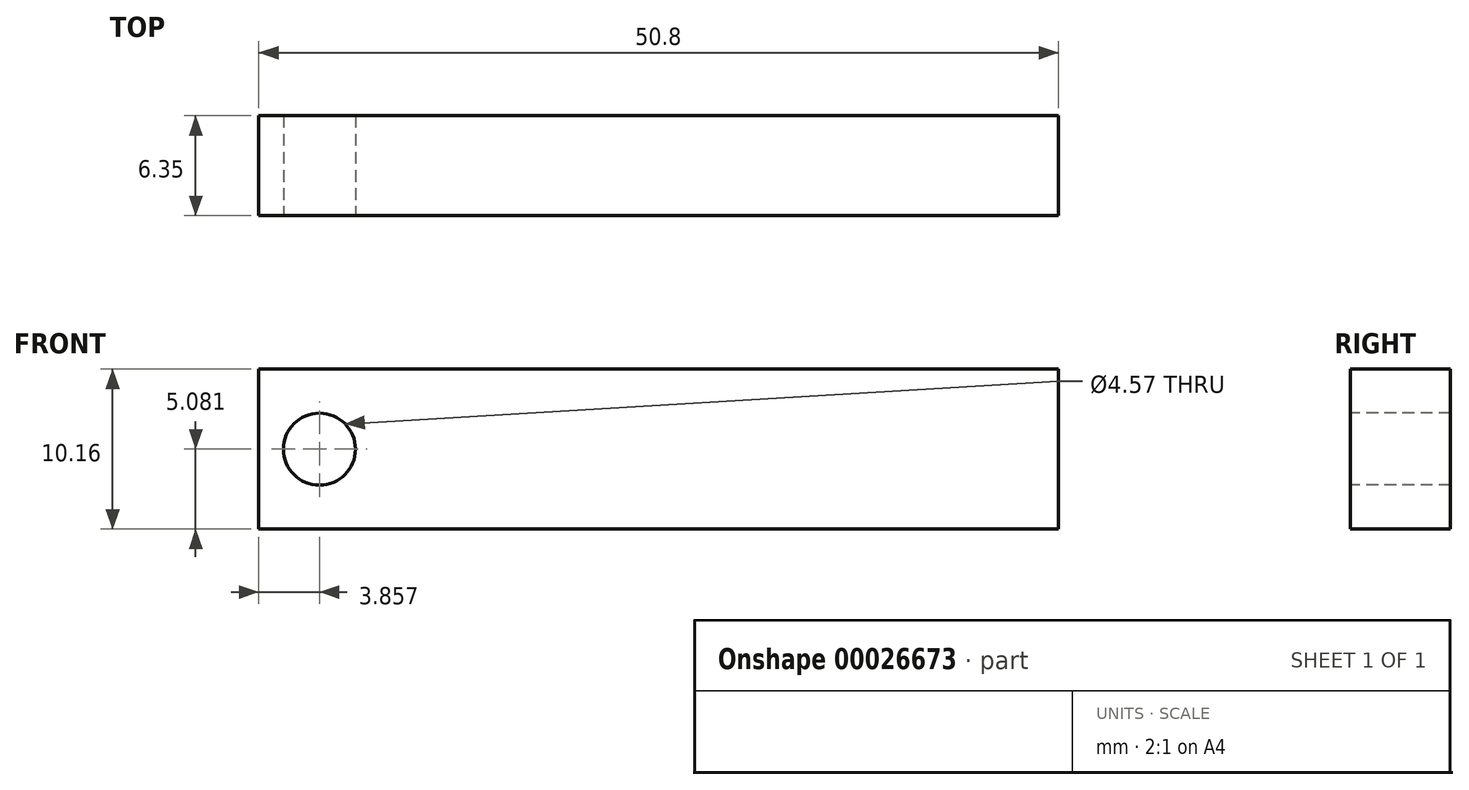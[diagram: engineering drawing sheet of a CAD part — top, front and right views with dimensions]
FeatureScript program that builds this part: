
annotation { "Feature Type Name" : "Feature", "Feature Type Description" : "" }
export const myFeature = defineFeature(function(context is Context, id is Id, definition is map)
    precondition{}
    {
        {
            var Q0;
            Q0=qCreatedBy(makeId("Front.planeOp"),FACE);
            var sketch = newSketch(context, id + "F0", { "sketchPlane" : qUnion([Q0])});
            skLineSegment(sketch, "E0.bottom", {"start": v(-21.08, 0.22) * mm, "end": v(29.72, 0.22) * mm});
            skLineSegment(sketch, "E0.top", {"start": v(-21.08, -9.94) * mm, "end": v(29.72, -9.94) * mm});
            skLineSegment(sketch, "E0.left", {"start": v(-21.08, 0.22) * mm, "end": v(-21.08, -9.94) * mm});
            skLineSegment(sketch, "E0.right", {"start": v(29.72, 0.22) * mm, "end": v(29.72, -9.94) * mm});
            skSolve(sketch);
        }
        {
            var Q0;
            Q0 = qSketchRegion(id + "F0", true);
            extrude(context, id + "F1", {"entities" : qUnion([Q0]), "depth" : 6.35 * mm});
        }
        {
            var Q0;
            Q0=makeQuery(id+"F1.opExtrude","CAP_FACE",FACE,{"disambiguationData":[OSD([sQuery(id+"F0.wireOp",EDGE,"E0.bottom"),sQuery(id+"F0.wireOp",EDGE,"E0.top"),sQuery(id+"F0.wireOp",EDGE,"E0.left"),sQuery(id+"F0.wireOp",EDGE,"E0.right")])],"isStart":false});
            var sketch = newSketch(context, id + "F2", { "sketchPlane" : qUnion([Q0])});
            skCircle(sketch, "E1", {"center": v(-17.22, -4.86) * mm, "radius": 2.29 * mm});
            skSolve(sketch);
        }
        {
            var Q0;
            Q0 = qSketchRegion(id + "F2", true);
            extrude(context, id + "F3", {"entities" : qUnion([Q0]), "operationType" : NewBodyOperationType.REMOVE, "oppositeDirection" : true, "depth" : 25.4 * mm});
        }
    });
